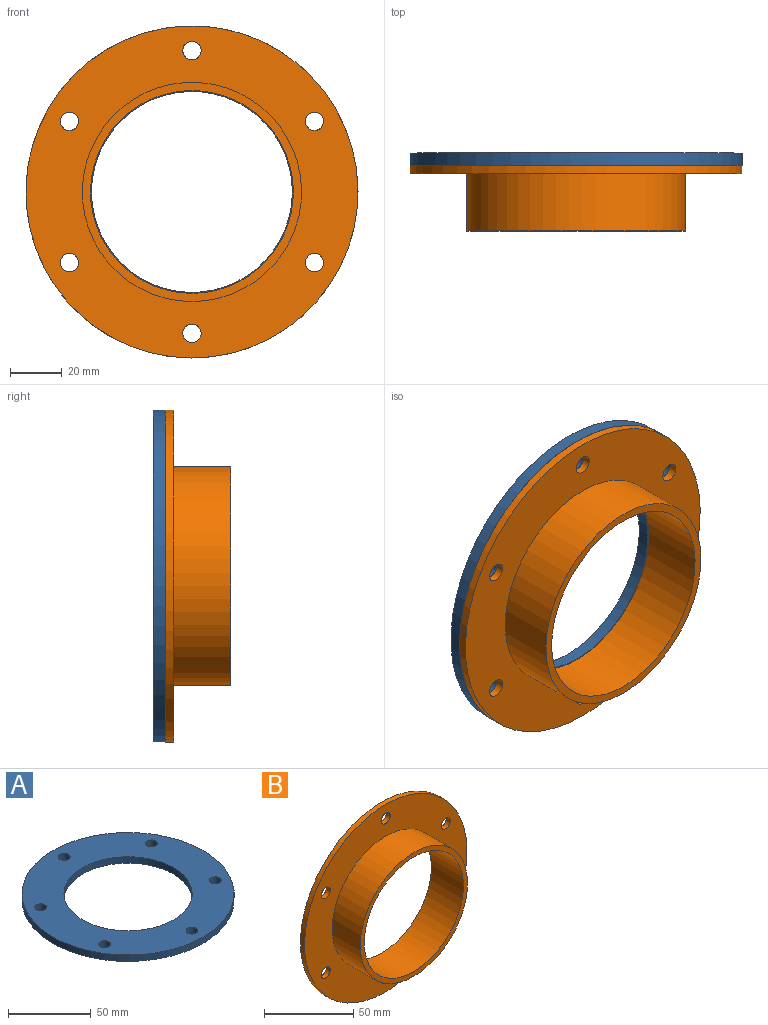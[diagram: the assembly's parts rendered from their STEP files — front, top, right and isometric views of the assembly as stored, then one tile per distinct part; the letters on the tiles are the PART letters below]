
ASSEMBLY  parts=2 mates=1
PART A: 10 faces, bbox 128.5x128.5x4.8 mm
  f0: cylinder r=3.57mm len=7.14mm, axis (0,0,-1), area 106.9mm2, adj f8,f9
  f1: cylinder r=3.57mm len=7.14mm, axis (0,0,-1), area 106.9mm2, adj f8,f9
  f2: cylinder r=3.57mm len=7.14mm, axis (0,0,-1), area 106.9mm2, adj f8,f9
  f3: cylinder r=3.57mm len=7.14mm, axis (0,0,-1), area 106.9mm2, adj f8,f9
  f4: cylinder r=3.57mm len=7.14mm, axis (0,0,-1), area 106.9mm2, adj f8,f9
  f5: cylinder r=38.86mm len=77.72mm, axis (0,0,-1), area 1162.9mm2, adj f8,f9
  f6: cylinder r=3.57mm len=7.14mm, axis (0,0,-1), area 106.9mm2, adj f8,f9
  f7: cylinder r=64.26mm len=128.52mm, axis (0,0,-1), area 1923mm2, adj f8,f9
  f8: plane 128.52x128.52mm, normal (0,0,1), area 7988.4mm2, adj f0,f1,f2,f3,f4,f5,f6,f7
  f9: plane 128.52x128.52mm, normal (0,0,-1), area 7988.4mm2, adj f0,f1,f2,f3,f4,f5,f6,f7
PART B: 12 faces, bbox 128.5x25.4x128.5 mm
  f0: cylinder r=3.57mm len=7.14mm, axis (0,1,0), area 71.3mm2, adj f7,f8
  f1: cylinder r=3.57mm len=7.14mm, axis (0,1,0), area 71.3mm2, adj f7,f8
  f2: cylinder r=3.57mm len=7.14mm, axis (0,1,0), area 71.3mm2, adj f7,f8
  f3: cylinder r=3.57mm len=7.14mm, axis (0,1,0), area 71.3mm2, adj f7,f8
  f4: cylinder r=3.57mm len=7.14mm, axis (0,1,0), area 71.3mm2, adj f7,f8
  f5: cylinder r=3.57mm len=7.14mm, axis (0,1,0), area 71.3mm2, adj f7,f8
  f6: cylinder r=64.26mm len=128.52mm, axis (0,1,0), area 1282mm2, adj f7,f8
  f7: plane 128.52x128.52mm, normal (0,-1,0), area 7080.4mm2, adj f0,f1,f2,f3,f4,f5,f6,f10
  f8: plane 128.52x128.52mm, normal (0,1,0), area 7895mm2, adj f0,f1,f2,f3,f4,f5,f6,f9
  f9: cylinder r=39.24mm len=78.49mm, axis (0,1,0), area 6262.9mm2, adj f8,f11
  f10: cylinder r=42.42mm len=84.84mm, axis (0,1,0), area 5923.4mm2, adj f7,f11
  f11: plane 84.84x84.84mm, normal (0,-1,0), area 814.5mm2, adj f9,f10
PLACE A rot(axis=(-1,0,0),90deg) t=(-23.46,-9.7,-13.28)mm
PLACE B t=(-23.46,-9.7,-13.28)mm
MATE fastened A.f5 <-> B.f6  axis (0,-1,0) through (-23.46,-9.7,-13.28)mm
